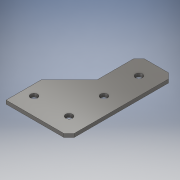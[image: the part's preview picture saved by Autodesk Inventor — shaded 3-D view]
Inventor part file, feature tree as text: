
AUTODESK INVENTOR PART (.ipt)
format: ipt  version: 2017 (Build 210142000, 142)  size: 109,056 bytes
history: native  units: in
note: dims shown in document units (in); Inventor stores cm internally (conversion verified against a paired STEP export)
features: extrude x1, sketch x1
ambient origin geometry x8: Origin, YZ Plane, XZ Plane, XY Plane, X Axis, Y Axis, Z Axis, Center Point
bodies: Body1 (feature_tree)
feature tree (2):
  extrude  "Extrusion2"  [1 undecoded]
  sketch  "Sketch1"  dims[d26=0.1in d27=0.0in]
note: 1 required parameter value undecoded (feature->parameter linkage not recoverable at this tier; creation-order binding heuristic only, values carry confidence <= 0.55)
